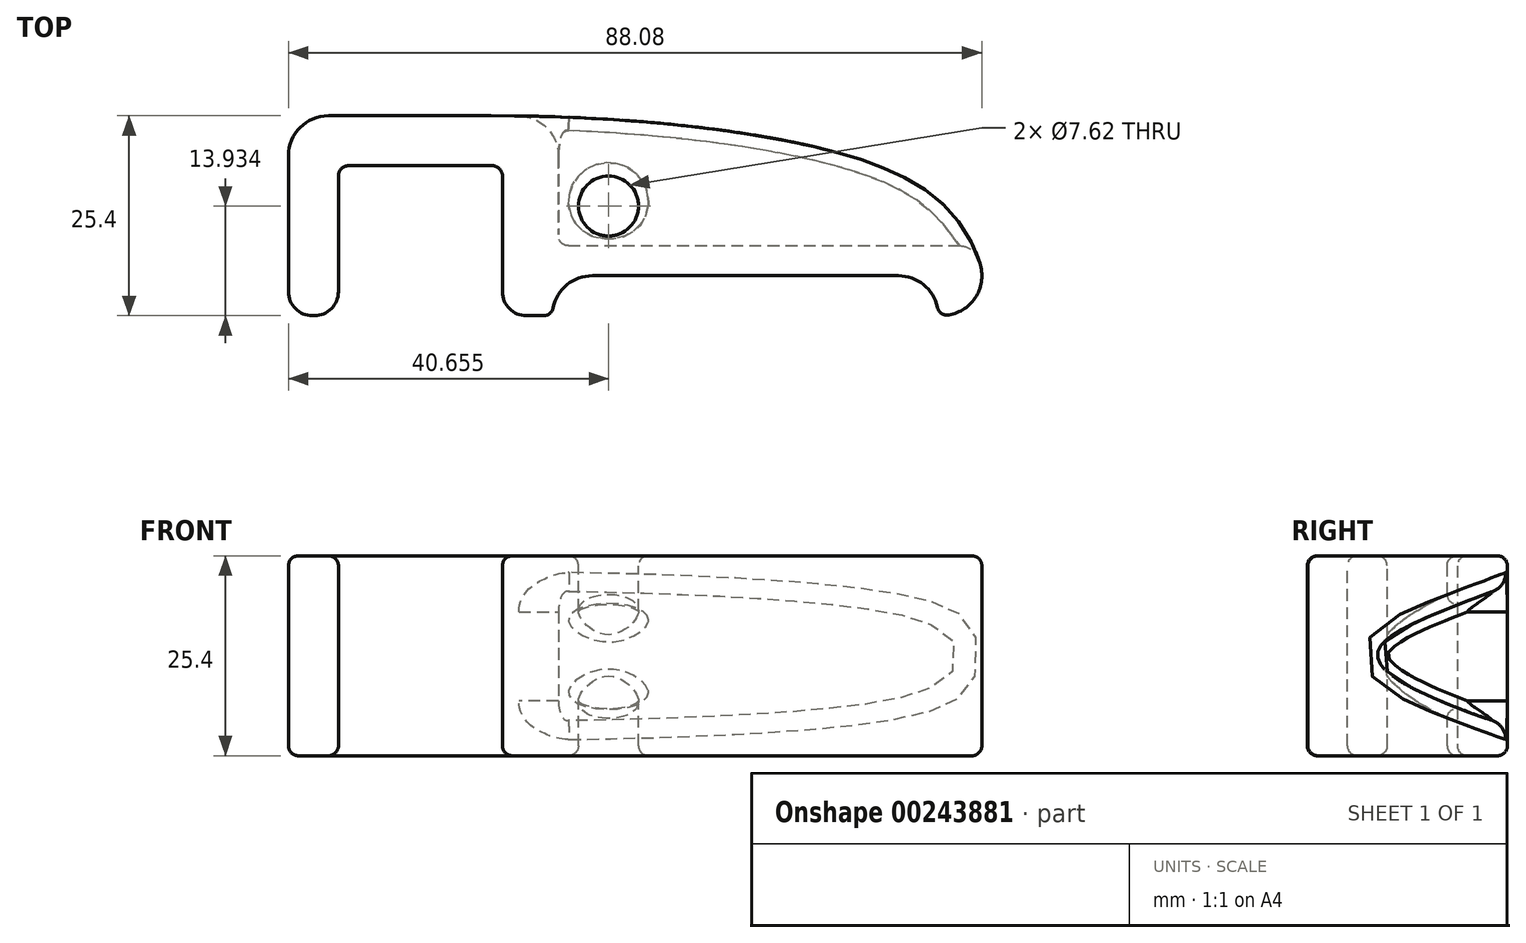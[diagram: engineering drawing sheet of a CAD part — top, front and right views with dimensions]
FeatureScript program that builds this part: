
annotation { "Feature Type Name" : "Feature", "Feature Type Description" : "" }
export const myFeature = defineFeature(function(context is Context, id is Id, definition is map)
    precondition{}
    {
        {
            var Q0;
            Q0=qCreatedBy(makeId("Top.planeOp"),FACE);
            var sketch = newSketch(context, id + "F0", { "sketchPlane" : qUnion([Q0])});
            skLineSegment(sketch, "E0", {"start": v(0, 0) * mm, "end": v(0, -25.4) * mm});
            skLineSegment(sketch, "E1", {"start": v(0, -25.4) * mm, "end": v(6.35, -25.4) * mm});
            skLineSegment(sketch, "E2", {"start": v(6.35, -25.4) * mm, "end": v(6.35, -6.35) * mm});
            skLineSegment(sketch, "E3", {"start": v(6.35, -6.35) * mm, "end": v(27.18, -6.35) * mm});
            skLineSegment(sketch, "E4", {"start": v(27.18, -6.35) * mm, "end": v(27.18, -25.4) * mm});
            skLineSegment(sketch, "E5", {"start": v(27.18, -25.4) * mm, "end": v(88.9, -25.4) * mm});
            skLineSegment(sketch, "E6", {"start": v(88.9, -25.4) * mm, "end": v(88.9, 0) * mm});
            skLineSegment(sketch, "E7", {"start": v(88.9, 0) * mm, "end": v(0, 0) * mm});
            skFitSpline(sketch, "E8", {"points": [v(25.73, 0) * mm, v(69.73, -4.7) * mm, v(84.63, -12.83) * mm, v(88.9, -25.4) * mm], "startDerivative": vector(108.81, 0) * mm, "endDerivative": vector(0, -54) * mm});
            skSolve(sketch);
        }
        {
            var Q0;
            {var subQ2=sQuery(id+"F0.wireOp",EDGE,"E0");Q0=makeQuery(id+"F0.imprint","IMPRINT",FACE,{"disambiguationData":[TD([[makeQuery(id+"F0.imprint","IMPRINT",EDGE,{"derivedFrom":subQ2}),1.0]])]});}
            extrude(context, id + "F1", {"entities" : qUnion([Q0]), "depth" : 25.4 * mm});
        }
        {
            var Q0;
            Q0=makeQuery(id+"F1.opExtrude","CAP_VERTEX",VERTEX,{"disambiguationData":[OSD([sQuery(id+"F0.wireOp",EDGE,"E5"),sQuery(id+"F0.wireOp",EDGE,"E6"),sQuery(id+"F0.wireOp",EDGE,"E8")])],"isStart":false});
            var Q1;
            Q1=qCreatedBy(makeId("Right.planeOp"),FACE);
            cPlane(context, id + "F2", {"entities" : qUnion([Q0, Q1]), "cplaneType" : CPlaneType.PLANE_POINT, "offset" : 152.4 * mm, "width" : 152.4 * mm, "height" : 152.4 * mm});
        }
        {
            var Q0;
            Q0=qCreatedBy(id+"F2.planeOp",FACE);
            var sketch = newSketch(context, id + "F3", { "sketchPlane" : qUnion([Q0])});
            skLineSegment(sketch, "E9.0.1", {"start": v(0, 0) * mm, "end": v(0, 25.4) * mm});
            skLineSegment(sketch, "E9.0.3", {"start": v(-25.4, 25.4) * mm, "end": v(-25.4, 0) * mm});
            skFitSpline(sketch, "E10", {"points": [v(0, 21.6) * mm, v(-16.51, 12.7) * mm, v(0, 3.81) * mm], "startDerivative": vector(-56.73, -21.7) * mm, "endDerivative": vector(53.72, -18.15) * mm});
            skLineSegment(sketch, "E11", {"start": v(0, 12.7) * mm, "end": v(-16.51, 12.7) * mm, "construction": true});
            skSolve(sketch);
        }
        {
            var Q0;
            Q0=qSketchRegion(id+"F3",true);
            extrude(context, id + "F4", {"entities" : qUnion([Q0]), "operationType" : NewBodyOperationType.REMOVE, "oppositeDirection" : true, "depth" : 54.6 * mm});
        }
        {
            var Q0;
            Q0=makeQuery(id+"F1.opExtrude","CAP_FACE",FACE,{"disambiguationData":[OSD([sQuery(id+"F0.wireOp",EDGE,"E0"),sQuery(id+"F0.wireOp",EDGE,"E1"),sQuery(id+"F0.wireOp",EDGE,"E2"),sQuery(id+"F0.wireOp",EDGE,"E3"),sQuery(id+"F0.wireOp",EDGE,"E4"),sQuery(id+"F0.wireOp",EDGE,"E5"),sQuery(id+"F0.wireOp",EDGE,"E7"),sQuery(id+"F0.wireOp",EDGE,"E8")])],"isStart":false});
            var sketch = newSketch(context, id + "F5", { "sketchPlane" : qUnion([Q0])});
            skCircle(sketch, "E12", {"center": v(40.66, -11.47) * mm, "radius": 3.81 * mm});
            skSolve(sketch);
        }
        {
            var Q0;
            Q0=qSketchRegion(id+"F5",true);
            extrude(context, id + "F6", {"entities" : qUnion([Q0]), "operationType" : NewBodyOperationType.REMOVE, "endBound" : BoundingType.THROUGH_ALL, "oppositeDirection" : true, "depth" : 25.4 * mm});
        }
        {
            var Q0;
            Q0=makeQuery(id+"F1.opExtrude","CAP_FACE",FACE,{"disambiguationData":[OSD([sQuery(id+"F0.wireOp",EDGE,"E0"),sQuery(id+"F0.wireOp",EDGE,"E1"),sQuery(id+"F0.wireOp",EDGE,"E2"),sQuery(id+"F0.wireOp",EDGE,"E3"),sQuery(id+"F0.wireOp",EDGE,"E4"),sQuery(id+"F0.wireOp",EDGE,"E5"),sQuery(id+"F0.wireOp",EDGE,"E7"),sQuery(id+"F0.wireOp",EDGE,"E8")])],"isStart":false});
            var sketch = newSketch(context, id + "F7", { "sketchPlane" : qUnion([Q0])});
            skLineSegment(sketch, "E13", {"start": v(82.55, -20.32) * mm, "end": v(33.53, -20.32) * mm});
            skLineSegment(sketch, "E14", {"start": v(33.53, -20.32) * mm, "end": v(33.53, -25.4) * mm});
            skLineSegment(sketch, "E15", {"start": v(82.55, -20.32) * mm, "end": v(82.55, -25.4) * mm});
            skSolve(sketch);
        }
        {
            var Q0;
            Q0=qSketchRegion(id+"F7",true);
            var Q1;
            Q1=makeQuery(id+"F7.imprint","IMPRINT",FACE,{"disambiguationData":[TD([[makeQuery(id+"F7.imprint","IMPRINT",EDGE,{"derivedFrom":sQuery(id+"F7.wireOp",EDGE,"E13")}),1.0]])]});
            extrude(context, id + "F8", {"entities" : qUnion([Q0, Q1]), "operationType" : NewBodyOperationType.REMOVE, "endBound" : BoundingType.THROUGH_ALL, "oppositeDirection" : true, "depth" : 25.4 * mm});
        }
        {
            var Q0;
            Q0=makeQuery(id+"F4.boolean.opBoolean","INTERSECT",EDGE,{"derivedFrom":[makeQuery(id+"F1.opExtrude","SWEPT_FACE",FACE,{"disambiguationData":[OSD([sQuery(id+"F0.wireOp",EDGE,"E8")])]}),makeQuery(id+"F4.opExtrude","SWEPT_FACE",FACE,{"disambiguationData":[OSD([sQuery(id+"F3.wireOp",EDGE,"E10")])]})]});
            fillet(context, id + "F9", {"entities" : qUnion([Q0]), "radius" : 2.54 * mm, "tangentPropagation" : true, "allowEdgeOverflow" : false});
        }
        {
            var Q0;
            Q0=makeQuery(id+"F1.opExtrude","SWEPT_EDGE",EDGE,{"disambiguationData":[OSD([sQuery(id+"F0.wireOp",EDGE,"E5"),sQuery(id+"F0.wireOp",EDGE,"E6"),sQuery(id+"F0.wireOp",EDGE,"E8")])]});
            var Q1;
            Q1=makeQuery(id+"F1.opExtrude","SWEPT_EDGE",EDGE,{"disambiguationData":[OSD([sQuery(id+"F0.wireOp",EDGE,"E0"),sQuery(id+"F0.wireOp",EDGE,"E7")])]});
            fillet(context, id + "F10", {"entities" : qUnion([Q0, Q1]), "radius" : 5.08 * mm, "tangentPropagation" : true, "allowEdgeOverflow" : false});
        }
        {
            var Q0;
            Q0=makeQuery(id+"F1.opExtrude","SWEPT_EDGE",EDGE,{"disambiguationData":[OSD([sQuery(id+"F0.wireOp",EDGE,"E4"),sQuery(id+"F0.wireOp",EDGE,"E5")])]});
            var Q1;
            Q1=makeQuery(id+"F1.opExtrude","SWEPT_EDGE",EDGE,{"disambiguationData":[OSD([sQuery(id+"F0.wireOp",EDGE,"E1"),sQuery(id+"F0.wireOp",EDGE,"E2")])]});
            var Q2;
            Q2=makeQuery(id+"F1.opExtrude","SWEPT_EDGE",EDGE,{"disambiguationData":[OSD([sQuery(id+"F0.wireOp",EDGE,"E0"),sQuery(id+"F0.wireOp",EDGE,"E1")])]});
            fillet(context, id + "F11", {"entities" : qUnion([Q0, Q1, Q2]), "radius" : 3.05 * mm, "tangentPropagation" : true, "allowEdgeOverflow" : false});
        }
        {
            var Q0;
            Q0=makeQuery(id+"F4.boolean.opBoolean","COPY",EDGE,{"derivedFrom":makeQuery(id+"F4.opExtrude","CAP_EDGE",EDGE,{"disambiguationData":[OSD([sQuery(id+"F3.wireOp",EDGE,"E10")])],"isStart":false})});
            fillet(context, id + "F12", {"entities" : qUnion([Q0]), "radius" : 1.27 * mm, "tangentPropagation" : true, "allowEdgeOverflow" : false});
        }
        {
            var Q0;
            Q0=makeQuery(id+"F4.boolean.opBoolean","INTERSECT",EDGE,{"derivedFrom":[makeQuery(id+"F1.opExtrude","SWEPT_FACE",FACE,{"disambiguationData":[OSD([sQuery(id+"F0.wireOp",EDGE,"E8")])]}),makeQuery(id+"F4.opExtrude","CAP_FACE",FACE,{"disambiguationData":[OSD([sQuery(id+"F3.wireOp",EDGE,"E9.0.1"),sQuery(id+"F3.wireOp",EDGE,"E10")])],"isStart":false})]});
            fillet(context, id + "F13", {"entities" : qUnion([Q0]), "radius" : 5.08 * mm, "tangentPropagation" : true, "allowEdgeOverflow" : false});
        }
        {
            var Q0;
            Q0=makeQuery(id+"F1.opExtrude","SWEPT_EDGE",EDGE,{"disambiguationData":[OSD([sQuery(id+"F0.wireOp",EDGE,"E2"),sQuery(id+"F0.wireOp",EDGE,"E3")])]});
            var Q1;
            Q1=makeQuery(id+"F1.opExtrude","SWEPT_EDGE",EDGE,{"disambiguationData":[OSD([sQuery(id+"F0.wireOp",EDGE,"E3"),sQuery(id+"F0.wireOp",EDGE,"E4")])]});
            fillet(context, id + "F14", {"entities" : qUnion([Q0, Q1]), "radius" : 1.27 * mm, "tangentPropagation" : true, "allowEdgeOverflow" : false});
        }
        {
            var Q0;
            Q0=makeQuery(id+"F6.boolean.opBoolean","INTERSECT",EDGE,{"derivedFrom":[makeQuery(id+"F4.boolean.opBoolean","COPY",FACE,{"derivedFrom":makeQuery(id+"F4.opExtrude","SWEPT_FACE",FACE,{"disambiguationData":[OSD([sQuery(id+"F3.wireOp",EDGE,"E10")])]})}),makeQuery(id+"F6.opExtrude","SWEPT_FACE",FACE,{"disambiguationData":[OSD([sQuery(id+"F5.wireOp",EDGE,"E12")])]})]});
            fillet(context, id + "F15", {"entities" : qUnion([Q0]), "radius" : 1.27 * mm, "tangentPropagation" : true, "allowEdgeOverflow" : false});
        }
        {
            var Q0;
            Q0=makeQuery(id+"F8.boolean.opBoolean","COPY",EDGE,{"derivedFrom":makeQuery(id+"F8.opExtrude","SWEPT_EDGE",EDGE,{"disambiguationData":[OSD([sQuery(id+"F7.wireOp",EDGE,"E13"),sQuery(id+"F7.wireOp",EDGE,"E14")])]})});
            var Q1;
            Q1=makeQuery(id+"F8.boolean.opBoolean","COPY",EDGE,{"derivedFrom":makeQuery(id+"F8.opExtrude","SWEPT_EDGE",EDGE,{"disambiguationData":[OSD([sQuery(id+"F7.wireOp",EDGE,"E13"),sQuery(id+"F7.wireOp",EDGE,"E15")])]})});
            fillet(context, id + "F16", {"entities" : qUnion([Q0, Q1]), "radius" : 5.08 * mm, "tangentPropagation" : true, "allowEdgeOverflow" : false});
        }
        {
            var Q0;
            {var subQ0=sQuery(id+"F7.wireOp",EDGE,"E15");var subQ1=sQuery(id+"F0.wireOp",EDGE,"E5");var subQ2=sQuery(id+"F0.wireOp",EDGE,"E8");Q0=makeQuery(id+"F16.opFillet","BLEND_EDGE",EDGE,{"blendedFrom":[makeQuery(id+"F8.boolean.opBoolean","COPY",EDGE,{"derivedFrom":makeQuery(id+"F8.opExtrude","SWEPT_EDGE",EDGE,{"disambiguationData":[OSD([sQuery(id+"F7.wireOp",EDGE,"E13"),subQ0])]})}),makeQuery(id+"F8.boolean.opBoolean","SPLIT",FACE,{"disambiguationData":[TD([makeQuery(id+"F1.opExtrude","SWEPT_FACE",FACE,{"disambiguationData":[OSD([subQ2])]})])],"derivedFrom":makeQuery(id+"F1.opExtrude","SWEPT_FACE",FACE,{"disambiguationData":[OSD([subQ1])]})})],"blendedInto":[makeQuery(id+"F8.boolean.opBoolean","SPLIT",FACE,{"disambiguationData":[TD([makeQuery(id+"F1.opExtrude","SWEPT_FACE",FACE,{"disambiguationData":[OSD([subQ2])]})])],"derivedFrom":makeQuery(id+"F1.opExtrude","SWEPT_FACE",FACE,{"disambiguationData":[OSD([subQ1])]})})]});}
            var Q1;
            {var subQ0=sQuery(id+"F7.wireOp",EDGE,"E14");var subQ1=sQuery(id+"F0.wireOp",EDGE,"E5");var subQ2=sQuery(id+"F0.wireOp",EDGE,"E4");Q1=makeQuery(id+"F16.opFillet","BLEND_EDGE",EDGE,{"blendedFrom":[makeQuery(id+"F8.boolean.opBoolean","COPY",EDGE,{"derivedFrom":makeQuery(id+"F8.opExtrude","SWEPT_EDGE",EDGE,{"disambiguationData":[OSD([sQuery(id+"F7.wireOp",EDGE,"E13"),subQ0])]})}),makeQuery(id+"F8.boolean.opBoolean","SPLIT",FACE,{"disambiguationData":[TD([makeQuery(id+"F1.opExtrude","SWEPT_FACE",FACE,{"disambiguationData":[OSD([subQ2])]})])],"derivedFrom":makeQuery(id+"F1.opExtrude","SWEPT_FACE",FACE,{"disambiguationData":[OSD([subQ1])]})})],"blendedInto":[makeQuery(id+"F8.boolean.opBoolean","SPLIT",FACE,{"disambiguationData":[TD([makeQuery(id+"F1.opExtrude","SWEPT_FACE",FACE,{"disambiguationData":[OSD([subQ2])]})])],"derivedFrom":makeQuery(id+"F1.opExtrude","SWEPT_FACE",FACE,{"disambiguationData":[OSD([subQ1])]})})]});}
            fillet(context, id + "F17", {"entities" : qUnion([Q0, Q1]), "radius" : 1.27 * mm, "tangentPropagation" : true, "allowEdgeOverflow" : false});
        }
        {
            var Q0;
            Q0=makeQuery(id+"F1.opExtrude","CAP_FACE",FACE,{"disambiguationData":[OSD([sQuery(id+"F0.wireOp",EDGE,"E0"),sQuery(id+"F0.wireOp",EDGE,"E1"),sQuery(id+"F0.wireOp",EDGE,"E2"),sQuery(id+"F0.wireOp",EDGE,"E3"),sQuery(id+"F0.wireOp",EDGE,"E4"),sQuery(id+"F0.wireOp",EDGE,"E5"),sQuery(id+"F0.wireOp",EDGE,"E7"),sQuery(id+"F0.wireOp",EDGE,"E8")])],"isStart":false});
            var Q1;
            Q1=makeQuery(id+"F1.opExtrude","CAP_FACE",FACE,{"disambiguationData":[OSD([sQuery(id+"F0.wireOp",EDGE,"E0"),sQuery(id+"F0.wireOp",EDGE,"E1"),sQuery(id+"F0.wireOp",EDGE,"E2"),sQuery(id+"F0.wireOp",EDGE,"E3"),sQuery(id+"F0.wireOp",EDGE,"E4"),sQuery(id+"F0.wireOp",EDGE,"E5"),sQuery(id+"F0.wireOp",EDGE,"E7"),sQuery(id+"F0.wireOp",EDGE,"E8")])],"isStart":true});
            fillet(context, id + "F18", {"entities" : qUnion([Q0, Q1]), "radius" : 1.27 * mm, "tangentPropagation" : true, "allowEdgeOverflow" : false});
        }
    });
